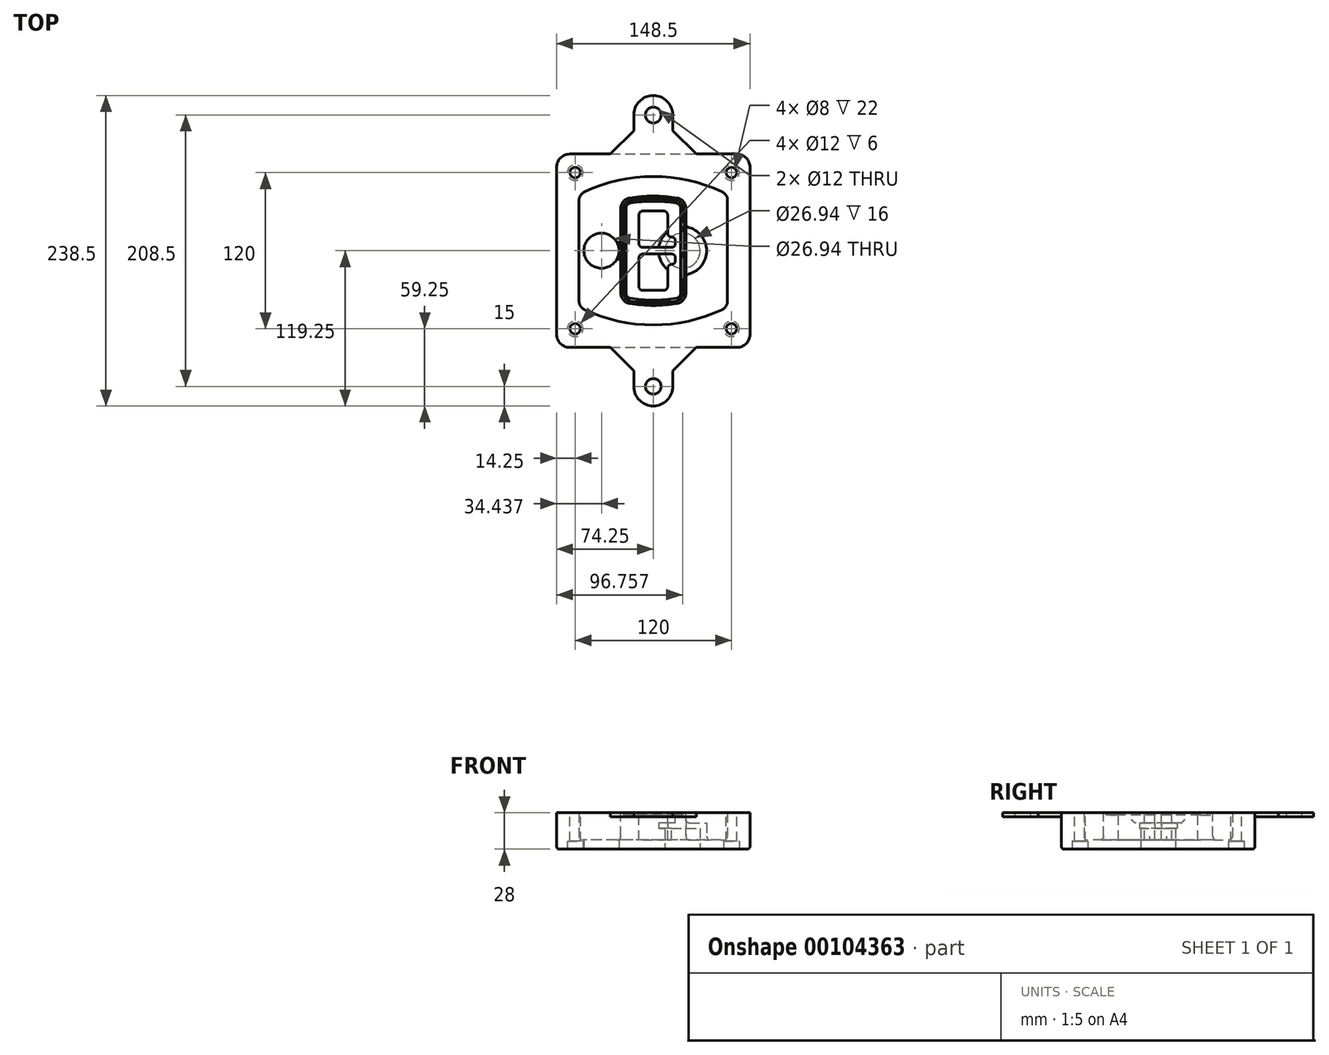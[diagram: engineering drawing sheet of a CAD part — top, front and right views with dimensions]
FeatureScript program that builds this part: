
annotation { "Feature Type Name" : "Feature", "Feature Type Description" : "" }
export const myFeature = defineFeature(function(context is Context, id is Id, definition is map)
    precondition{}
    {
        {
            var Q0;
            Q0=qCreatedBy(makeId("Top.planeOp"),FACE);
            var sketch = newSketch(context, id + "F0", { "sketchPlane" : qUnion([Q0])});
            skPoint(sketch, "E0.rect.middle", {"position": v(0, 0) * mm});
            skLineSegment(sketch, "E1.bottom", {"start": v(-64.25, -74.25) * mm, "end": v(64.25, -74.25) * mm});
            skLineSegment(sketch, "E1.top", {"start": v(-64.25, 74.25) * mm, "end": v(64.25, 74.25) * mm});
            skLineSegment(sketch, "E1.left", {"start": v(-74.25, -64.25) * mm, "end": v(-74.25, 64.25) * mm});
            skLineSegment(sketch, "E1.right", {"start": v(74.25, -64.25) * mm, "end": v(74.25, 64.25) * mm});
            skLineSegment(sketch, "E2", {"start": v(-74.25, 74.25) * mm, "end": v(74.25, -74.25) * mm, "construction": true});
            skLineSegment(sketch, "E3", {"start": v(74.25, 74.25) * mm, "end": v(-74.25, -74.25) * mm, "construction": true});
            skCircle(sketch, "E4", {"center": v(-60, 60) * mm, "radius": 4 * mm});
            skCircle(sketch, "E5", {"center": v(60, 60) * mm, "radius": 4 * mm});
            skCircle(sketch, "E6", {"center": v(60, -60) * mm, "radius": 4 * mm});
            skCircle(sketch, "E7", {"center": v(-60, -60) * mm, "radius": 4 * mm});
            skLineSegment(sketch, "E8", {"start": v(-60, 60) * mm, "end": v(60, 60) * mm, "construction": true});
            skLineSegment(sketch, "E9", {"start": v(60, 60) * mm, "end": v(60, -60) * mm, "construction": true});
            skLineSegment(sketch, "E10", {"start": v(60, -60) * mm, "end": v(-60, -60) * mm, "construction": true});
            skLineSegment(sketch, "E11", {"start": v(-60, -60) * mm, "end": v(-60, 60) * mm, "construction": true});
            skLineSegment(sketch, "E12", {"start": v(-60, 38.83) * mm, "end": v(-60, -38.83) * mm});
            skLineSegment(sketch, "E13", {"start": v(60, 38.83) * mm, "end": v(60, -38.83) * mm});
            skArc(sketch, "E14", {"start": v(54.26, 47.88) * mm, "mid": v(0, 60) * mm, "end": v(-54.26, 47.88) * mm});
            skArc(sketch, "E15", {"start": v(-54.26, -47.88) * mm, "mid": v(0, -60) * mm, "end": v(54.26, -47.88) * mm});
            skLineSegment(sketch, "E16", {"start": v(-60, 0) * mm, "end": v(60, 0) * mm, "construction": true});
            skPoint(sketch, "E17.visualSharp", {"position": v(-60, -45) * mm});
            skArc(sketch, "E17.filletArc", {"start": v(-60, -38.83) * mm, "mid": v(-58.44, -44.2) * mm, "end": v(-54.26, -47.88) * mm});
            skPoint(sketch, "E18.visualSharp", {"position": v(-60, 45) * mm});
            skArc(sketch, "E18.filletArc", {"start": v(-54.26, 47.88) * mm, "mid": v(-58.44, 44.2) * mm, "end": v(-60, 38.83) * mm});
            skPoint(sketch, "E19.visualSharp", {"position": v(60, 45) * mm});
            skArc(sketch, "E19.filletArc", {"start": v(60, 38.83) * mm, "mid": v(58.44, 44.2) * mm, "end": v(54.26, 47.88) * mm});
            skPoint(sketch, "E20.visualSharp", {"position": v(60, -45) * mm});
            skArc(sketch, "E20.filletArc", {"start": v(54.26, -47.88) * mm, "mid": v(58.44, -44.2) * mm, "end": v(60, -38.83) * mm});
            skPoint(sketch, "E21.visualSharp", {"position": v(-74.25, 74.25) * mm});
            skArc(sketch, "E21.filletArc", {"start": v(-64.25, 74.25) * mm, "mid": v(-71.32, 71.32) * mm, "end": v(-74.25, 64.25) * mm});
            skPoint(sketch, "E22.visualSharp", {"position": v(74.25, 74.25) * mm});
            skArc(sketch, "E22.filletArc", {"start": v(74.25, 64.25) * mm, "mid": v(71.32, 71.32) * mm, "end": v(64.25, 74.25) * mm});
            skPoint(sketch, "E23.visualSharp", {"position": v(74.25, -74.25) * mm});
            skArc(sketch, "E23.filletArc", {"start": v(64.25, -74.25) * mm, "mid": v(71.32, -71.32) * mm, "end": v(74.25, -64.25) * mm});
            skPoint(sketch, "E24.visualSharp", {"position": v(-74.25, -74.25) * mm});
            skArc(sketch, "E24.filletArc", {"start": v(-74.25, -64.25) * mm, "mid": v(-71.32, -71.32) * mm, "end": v(-64.25, -74.25) * mm});
            skArc(sketch, "E25.0", {"start": v(57, 38.83) * mm, "mid": v(55.9, 42.58) * mm, "end": v(52.98, 45.17) * mm});
            skLineSegment(sketch, "E25.1", {"start": v(57, 38.83) * mm, "end": v(57, -38.83) * mm});
            skArc(sketch, "E25.2", {"start": v(52.98, -45.17) * mm, "mid": v(55.9, -42.58) * mm, "end": v(57, -38.83) * mm});
            skArc(sketch, "E25.3", {"start": v(-52.98, -45.17) * mm, "mid": v(0, -57) * mm, "end": v(52.98, -45.17) * mm});
            skArc(sketch, "E25.4", {"start": v(-57, -38.83) * mm, "mid": v(-55.9, -42.58) * mm, "end": v(-52.98, -45.17) * mm});
            skArc(sketch, "E25.5", {"start": v(52.98, 45.17) * mm, "mid": v(0, 57) * mm, "end": v(-52.98, 45.17) * mm});
            skLineSegment(sketch, "E25.6", {"start": v(-57, 38.83) * mm, "end": v(-57, -38.83) * mm});
            skArc(sketch, "E25.7", {"start": v(-52.98, 45.17) * mm, "mid": v(-55.9, 42.58) * mm, "end": v(-57, 38.83) * mm});
            skArc(sketch, "E26.0", {"start": v(-55.96, 51.5) * mm, "mid": v(-61.82, 46.33) * mm, "end": v(-64, 38.83) * mm});
            skArc(sketch, "E26.1", {"start": v(55.96, 51.5) * mm, "mid": v(0, 64) * mm, "end": v(-55.96, 51.5) * mm});
            skArc(sketch, "E26.2", {"start": v(64, 38.83) * mm, "mid": v(61.82, 46.33) * mm, "end": v(55.96, 51.5) * mm});
            skLineSegment(sketch, "E26.3", {"start": v(64, 38.83) * mm, "end": v(64, -38.83) * mm});
            skArc(sketch, "E26.4", {"start": v(55.96, -51.5) * mm, "mid": v(61.82, -46.33) * mm, "end": v(64, -38.83) * mm});
            skLineSegment(sketch, "E26.5", {"start": v(-64, 38.83) * mm, "end": v(-64, -38.83) * mm});
            skArc(sketch, "E26.6", {"start": v(-55.96, -51.5) * mm, "mid": v(0, -64) * mm, "end": v(55.96, -51.5) * mm});
            skArc(sketch, "E26.7", {"start": v(-64, -38.83) * mm, "mid": v(-61.82, -46.33) * mm, "end": v(-55.96, -51.5) * mm});
            skSolve(sketch);
        }
        {
            var Q0;
            Q0=makeQuery(id+"F0.imprint","IMPRINT",FACE,{"disambiguationData":[TD([[makeQuery(id+"F0.imprint","IMPRINT",EDGE,{"derivedFrom":sQuery(id+"F0.wireOp",EDGE,"E1.bottom")}),1.0]])]});
            var Q1;
            Q1=makeQuery(id+"F0.imprint","IMPRINT",FACE,{"disambiguationData":[TD([[makeQuery(id+"F0.imprint","IMPRINT",EDGE,{"derivedFrom":sQuery(id+"F0.wireOp",EDGE,"E12")}),1.0]])]});
            var Q2;
            Q2=makeQuery(id+"F0.imprint","IMPRINT",FACE,{"disambiguationData":[TD([[makeQuery(id+"F0.imprint","IMPRINT",EDGE,{"derivedFrom":sQuery(id+"F0.wireOp",EDGE,"E25.0")}),1.0]])]});
            var Q3;
            Q3=makeQuery(id+"F0.imprint","IMPRINT",FACE,{"disambiguationData":[TD([[makeQuery(id+"F0.imprint","IMPRINT",EDGE,{"derivedFrom":sQuery(id+"F0.wireOp",EDGE,"E12")}),-1.0]])]});
            extrude(context, id + "F1", {"entities" : qUnion([Q0, Q1, Q2, Q3]), "oppositeDirection" : true, "depth" : 25 * mm});
        }
        {
            var Q0;
            Q0=makeQuery(id+"F0.imprint","IMPRINT",FACE,{"disambiguationData":[TD([[makeQuery(id+"F0.imprint","IMPRINT",EDGE,{"derivedFrom":sQuery(id+"F0.wireOp",EDGE,"E12")}),1.0]])]});
            extrude(context, id + "F2", {"entities" : qUnion([Q0]), "operationType" : NewBodyOperationType.ADD, "depth" : 3 * mm});
        }
        {
            var Q0;
            Q0=makeQuery(id+"F0.imprint","IMPRINT",FACE,{"disambiguationData":[TD([[makeQuery(id+"F0.imprint","IMPRINT",EDGE,{"derivedFrom":sQuery(id+"F0.wireOp",EDGE,"E25.0")}),1.0]])]});
            extrude(context, id + "F3", {"entities" : qUnion([Q0]), "operationType" : NewBodyOperationType.REMOVE, "oppositeDirection" : true, "depth" : 18 * mm});
        }
        {
            var Q0;
            Q0=makeQuery(id+"F2.opExtrude","CAP_FACE",FACE,{"disambiguationData":[OSD([sQuery(id+"F0.wireOp",EDGE,"E12"),sQuery(id+"F0.wireOp",EDGE,"E13"),sQuery(id+"F0.wireOp",EDGE,"E14"),sQuery(id+"F0.wireOp",EDGE,"E15"),sQuery(id+"F0.wireOp",EDGE,"E17.filletArc"),sQuery(id+"F0.wireOp",EDGE,"E18.filletArc"),sQuery(id+"F0.wireOp",EDGE,"E19.filletArc"),sQuery(id+"F0.wireOp",EDGE,"E20.filletArc"),sQuery(id+"F0.wireOp",EDGE,"E25.0"),sQuery(id+"F0.wireOp",EDGE,"E25.1"),sQuery(id+"F0.wireOp",EDGE,"E25.2"),sQuery(id+"F0.wireOp",EDGE,"E25.3"),sQuery(id+"F0.wireOp",EDGE,"E25.4"),sQuery(id+"F0.wireOp",EDGE,"E25.5"),sQuery(id+"F0.wireOp",EDGE,"E25.6"),sQuery(id+"F0.wireOp",EDGE,"E25.7")])],"isStart":false});
            var sketch = newSketch(context, id + "F4", { "sketchPlane" : qUnion([Q0])});
            skArc(sketch, "E27.0", {"start": v(-18.34, -40.45) * mm, "mid": v(0, -42) * mm, "end": v(18.34, -40.45) * mm});
            skArc(sketch, "E28.0", {"start": v(18.34, 40.45) * mm, "mid": v(0, 42) * mm, "end": v(-18.34, 40.45) * mm});
            skLineSegment(sketch, "E29", {"start": v(-25, 32.57) * mm, "end": v(-25, -32.57) * mm});
            skLineSegment(sketch, "E30", {"start": v(25, 32.57) * mm, "end": v(25, -32.57) * mm});
            skLineSegment(sketch, "E31", {"start": v(-25, 39.1) * mm, "end": v(25, 39.1) * mm, "construction": true});
            skLineSegment(sketch, "E32", {"start": v(-25, -39.1) * mm, "end": v(25, -39.1) * mm, "construction": true});
            skPoint(sketch, "E33.visualSharp", {"position": v(-25, 39.1) * mm});
            skArc(sketch, "E33.filletArc", {"start": v(-18.34, 40.45) * mm, "mid": v(-23.11, 37.73) * mm, "end": v(-25, 32.57) * mm});
            skPoint(sketch, "E34.visualSharp", {"position": v(25, 39.1) * mm});
            skArc(sketch, "E34.filletArc", {"start": v(25, 32.57) * mm, "mid": v(23.11, 37.73) * mm, "end": v(18.34, 40.45) * mm});
            skPoint(sketch, "E35.visualSharp", {"position": v(25, -39.1) * mm});
            skArc(sketch, "E35.filletArc", {"start": v(18.34, -40.45) * mm, "mid": v(23.11, -37.73) * mm, "end": v(25, -32.57) * mm});
            skPoint(sketch, "E36.visualSharp", {"position": v(-25, -39.1) * mm});
            skArc(sketch, "E36.filletArc", {"start": v(-25, -32.57) * mm, "mid": v(-23.11, -37.73) * mm, "end": v(-18.34, -40.45) * mm});
            skArc(sketch, "E37.0", {"start": v(52.98, 45.17) * mm, "mid": v(0, 57) * mm, "end": v(-52.98, 45.17) * mm});
            skArc(sketch, "E37.1", {"start": v(-52.98, 45.17) * mm, "mid": v(-55.9, 42.58) * mm, "end": v(-57, 38.83) * mm});
            skLineSegment(sketch, "E37.2", {"start": v(-57, 38.83) * mm, "end": v(-57, -38.83) * mm});
            skArc(sketch, "E37.3", {"start": v(-57, -38.83) * mm, "mid": v(-55.9, -42.58) * mm, "end": v(-52.98, -45.17) * mm});
            skArc(sketch, "E37.4", {"start": v(-52.98, -45.17) * mm, "mid": v(0, -57) * mm, "end": v(52.98, -45.17) * mm});
            skArc(sketch, "E37.5", {"start": v(52.98, -45.17) * mm, "mid": v(55.9, -42.58) * mm, "end": v(57, -38.83) * mm});
            skLineSegment(sketch, "E37.6", {"start": v(57, 38.83) * mm, "end": v(57, -38.83) * mm});
            skArc(sketch, "E37.7", {"start": v(57, 38.83) * mm, "mid": v(55.9, 42.58) * mm, "end": v(52.98, 45.17) * mm});
            skLineSegment(sketch, "E38.0", {"start": v(23, 32.57) * mm, "end": v(23, -32.57) * mm});
            skArc(sketch, "E38.1", {"start": v(18, -38.48) * mm, "mid": v(21.58, -36.44) * mm, "end": v(23, -32.57) * mm});
            skArc(sketch, "E38.2", {"start": v(-18, -38.48) * mm, "mid": v(0, -40) * mm, "end": v(18, -38.48) * mm});
            skArc(sketch, "E38.3", {"start": v(-23, -32.57) * mm, "mid": v(-21.58, -36.44) * mm, "end": v(-18, -38.48) * mm});
            skLineSegment(sketch, "E38.4", {"start": v(-23, 32.57) * mm, "end": v(-23, -32.57) * mm});
            skArc(sketch, "E38.5", {"start": v(23, 32.57) * mm, "mid": v(21.58, 36.44) * mm, "end": v(18, 38.48) * mm});
            skArc(sketch, "E38.6", {"start": v(-18, 38.48) * mm, "mid": v(-21.58, 36.44) * mm, "end": v(-23, 32.57) * mm});
            skArc(sketch, "E38.7", {"start": v(18, 38.48) * mm, "mid": v(0, 40) * mm, "end": v(-18, 38.48) * mm});
            skArc(sketch, "E39.0", {"start": v(21, 32.57) * mm, "mid": v(20.06, 35.15) * mm, "end": v(17.67, 36.5) * mm});
            skLineSegment(sketch, "E39.1", {"start": v(21, 32.57) * mm, "end": v(21, -32.57) * mm});
            skArc(sketch, "E39.2", {"start": v(17.67, -36.5) * mm, "mid": v(20.06, -35.15) * mm, "end": v(21, -32.57) * mm});
            skArc(sketch, "E39.3", {"start": v(-17.67, -36.5) * mm, "mid": v(0, -38) * mm, "end": v(17.67, -36.5) * mm});
            skArc(sketch, "E39.4", {"start": v(-21, -32.57) * mm, "mid": v(-20.06, -35.15) * mm, "end": v(-17.67, -36.5) * mm});
            skArc(sketch, "E39.5", {"start": v(17.67, 36.5) * mm, "mid": v(0, 38) * mm, "end": v(-17.67, 36.5) * mm});
            skLineSegment(sketch, "E39.6", {"start": v(-21, 32.57) * mm, "end": v(-21, -32.57) * mm});
            skArc(sketch, "E39.7", {"start": v(-17.67, 36.5) * mm, "mid": v(-20.06, 35.15) * mm, "end": v(-21, 32.57) * mm});
            skLineSegment(sketch, "E40", {"start": v(-25, 0) * mm, "end": v(25, 0) * mm, "construction": true});
            skLineSegment(sketch, "E41", {"start": v(-11, 5.5) * mm, "end": v(-11, 27.5) * mm});
            skLineSegment(sketch, "E42", {"start": v(-8, 30.5) * mm, "end": v(8, 30.5) * mm});
            skLineSegment(sketch, "E43", {"start": v(11, 27.5) * mm, "end": v(11, 13.5) * mm});
            skLineSegment(sketch, "E44", {"start": v(14, 10.5) * mm, "end": v(14, 10.5) * mm});
            skLineSegment(sketch, "E45", {"start": v(17, 7.5) * mm, "end": v(17, 5.5) * mm});
            skLineSegment(sketch, "E46", {"start": v(14, 2.5) * mm, "end": v(-8, 2.5) * mm});
            skPoint(sketch, "E47.visualSharp", {"position": v(-11, 30.5) * mm});
            skArc(sketch, "E47.filletArc", {"start": v(-8, 30.5) * mm, "mid": v(-10.12, 29.62) * mm, "end": v(-11, 27.5) * mm});
            skPoint(sketch, "E48.visualSharp", {"position": v(11, 30.5) * mm});
            skArc(sketch, "E48.filletArc", {"start": v(11, 27.5) * mm, "mid": v(10.12, 29.62) * mm, "end": v(8, 30.5) * mm});
            skPoint(sketch, "E49.visualSharp", {"position": v(11, 10.5) * mm});
            skArc(sketch, "E49.filletArc", {"start": v(11, 13.5) * mm, "mid": v(11.88, 11.38) * mm, "end": v(14, 10.5) * mm});
            skPoint(sketch, "E50.visualSharp", {"position": v(17, 10.5) * mm});
            skArc(sketch, "E50.filletArc", {"start": v(17, 7.5) * mm, "mid": v(16.12, 9.62) * mm, "end": v(14, 10.5) * mm});
            skPoint(sketch, "E51.visualSharp", {"position": v(17, 2.5) * mm});
            skArc(sketch, "E51.filletArc", {"start": v(14, 2.5) * mm, "mid": v(16.12, 3.38) * mm, "end": v(17, 5.5) * mm});
            skPoint(sketch, "E52.visualSharp", {"position": v(-11, 2.5) * mm});
            skArc(sketch, "E52.filletArc", {"start": v(-11, 5.5) * mm, "mid": v(-10.12, 3.38) * mm, "end": v(-8, 2.5) * mm});
            skLineSegment(sketch, "E53.0.MirrorCS", {"start": v(14, -2.5) * mm, "end": v(-8, -2.5) * mm});
            skArc(sketch, "E54.0.MirrorCS", {"start": v(-11, -5.5) * mm, "mid": v(-10.12, -3.38) * mm, "end": v(-8, -2.5) * mm});
            skLineSegment(sketch, "E55.0.MirrorCS", {"start": v(-11, -5.5) * mm, "end": v(-11, -27.5) * mm});
            skArc(sketch, "E56.0.MirrorCS", {"start": v(-8, -30.5) * mm, "mid": v(-10.12, -29.62) * mm, "end": v(-11, -27.5) * mm});
            skLineSegment(sketch, "E57.0.MirrorCS", {"start": v(-8, -30.5) * mm, "end": v(8, -30.5) * mm});
            skArc(sketch, "E58.0.MirrorCS", {"start": v(11, -27.5) * mm, "mid": v(10.12, -29.62) * mm, "end": v(8, -30.5) * mm});
            skLineSegment(sketch, "E59.0.MirrorCS", {"start": v(11, -27.5) * mm, "end": v(11, -13.5) * mm});
            skArc(sketch, "E60.0.MirrorCS", {"start": v(11, -13.5) * mm, "mid": v(11.88, -11.38) * mm, "end": v(14, -10.5) * mm});
            skArc(sketch, "E61.0.MirrorCS", {"start": v(17, -7.5) * mm, "mid": v(16.12, -9.62) * mm, "end": v(14, -10.5) * mm});
            skLineSegment(sketch, "E62.0.MirrorCS", {"start": v(17, -7.5) * mm, "end": v(17, -5.5) * mm});
            skArc(sketch, "E63.0.MirrorCS", {"start": v(14, -2.5) * mm, "mid": v(16.12, -3.38) * mm, "end": v(17, -5.5) * mm});
            skSolve(sketch);
        }
        {
            var Q0;
            Q0=makeQuery(id+"F4.imprint","IMPRINT",FACE,{"disambiguationData":[TD([[makeQuery(id+"F4.imprint","IMPRINT",EDGE,{"derivedFrom":sQuery(id+"F4.wireOp",EDGE,"E27.0")}),1.0]])]});
            var Q1;
            Q1=makeQuery(id+"F4.imprint","IMPRINT",FACE,{"disambiguationData":[TD([[makeQuery(id+"F4.imprint","IMPRINT",EDGE,{"derivedFrom":sQuery(id+"F4.wireOp",EDGE,"E38.0")}),-1.0]])]});
            var Q2;
            Q2=makeQuery(id+"F4.imprint","IMPRINT",FACE,{"disambiguationData":[TD([[makeQuery(id+"F4.imprint","IMPRINT",EDGE,{"derivedFrom":sQuery(id+"F4.wireOp",EDGE,"E39.0")}),1.0]])]});
            extrude(context, id + "F5", {"entities" : qUnion([Q0, Q1, Q2]), "operationType" : NewBodyOperationType.ADD, "endBound" : BoundingType.UP_TO_NEXT, "oppositeDirection" : true, "depth" : 25 * mm});
        }
        {
            var Q0;
            Q0=makeQuery(id+"F4.imprint","IMPRINT",FACE,{"disambiguationData":[TD([[makeQuery(id+"F4.imprint","IMPRINT",EDGE,{"derivedFrom":sQuery(id+"F4.wireOp",EDGE,"E38.0")}),-1.0]])]});
            extrude(context, id + "F6", {"entities" : qUnion([Q0]), "operationType" : NewBodyOperationType.REMOVE, "oppositeDirection" : true, "depth" : 2 * mm});
        }
        {
            var Q0;
            Q0=makeQuery(id+"F1.opExtrude","CAP_FACE",FACE,{"disambiguationData":[OSD([sQuery(id+"F0.wireOp",EDGE,"E1.bottom"),sQuery(id+"F0.wireOp",EDGE,"E1.top"),sQuery(id+"F0.wireOp",EDGE,"E1.left"),sQuery(id+"F0.wireOp",EDGE,"E1.right"),sQuery(id+"F0.wireOp",EDGE,"E4"),sQuery(id+"F0.wireOp",EDGE,"E5"),sQuery(id+"F0.wireOp",EDGE,"E6"),sQuery(id+"F0.wireOp",EDGE,"E7"),sQuery(id+"F0.wireOp",EDGE,"E21.filletArc"),sQuery(id+"F0.wireOp",EDGE,"E22.filletArc"),sQuery(id+"F0.wireOp",EDGE,"E23.filletArc"),sQuery(id+"F0.wireOp",EDGE,"E24.filletArc")])],"isStart":false});
            var sketch = newSketch(context, id + "F7", { "sketchPlane" : qUnion([Q0])});
            skCircle(sketch, "E64", {"center": v(22.5, 0) * mm, "radius": 13.47 * mm});
            skCircle(sketch, "E65", {"center": v(-39.81, 0) * mm, "radius": 13.47 * mm});
            skLineSegment(sketch, "E66", {"start": v(74.25, 0) * mm, "end": v(-74.25, 0) * mm});
            skCircle(sketch, "E67", {"center": v(22.5, 0) * mm, "radius": 18.47 * mm});
            skCircle(sketch, "E68", {"center": v(60, -60) * mm, "radius": 6 * mm});
            skCircle(sketch, "E69", {"center": v(-60, -60) * mm, "radius": 6 * mm});
            skCircle(sketch, "E70", {"center": v(-60, 60) * mm, "radius": 6 * mm});
            skCircle(sketch, "E71", {"center": v(60, 60) * mm, "radius": 6 * mm});
            skSolve(sketch);
        }
        {
            var Q0;
            {var subQ1=sQuery(id+"F7.wireOp",EDGE,"E66");var subQ4=sQuery(id+"F7.wireOp",EDGE,"E64");var subQ6=makeQuery(id+"F7.imprint","INTERSECT",VERTEX,{"disambiguationData":[OD(0.0)],"derivedFrom":[subQ4,subQ1]});Q0=makeQuery(id+"F7.imprint","IMPRINT",FACE,{"disambiguationData":[TD([[makeQuery(id+"F7.imprint","IMPRINT",EDGE,{"disambiguationData":[TD([[subQ6,-1.0]])],"derivedFrom":subQ4}),-1.0]])]});}
            var Q1;
            {var subQ0=sQuery(id+"F7.wireOp",EDGE,"E66");var subQ1=sQuery(id+"F7.wireOp",EDGE,"E64");var subQ3=makeQuery(id+"F7.imprint","INTERSECT",VERTEX,{"disambiguationData":[OD(0.0)],"derivedFrom":[subQ1,subQ0]});Q1=makeQuery(id+"F7.imprint","IMPRINT",FACE,{"disambiguationData":[TD([[makeQuery(id+"F7.imprint","IMPRINT",EDGE,{"disambiguationData":[TD([[subQ3,-1.0]])],"derivedFrom":subQ1}),1.0]])]});}
            var Q2;
            {var subQ0=sQuery(id+"F7.wireOp",EDGE,"E66");var subQ1=sQuery(id+"F7.wireOp",EDGE,"E64");var subQ3=makeQuery(id+"F7.imprint","INTERSECT",VERTEX,{"disambiguationData":[OD(0.0)],"derivedFrom":[subQ1,subQ0]});Q2=makeQuery(id+"F7.imprint","IMPRINT",FACE,{"disambiguationData":[TD([[makeQuery(id+"F7.imprint","IMPRINT",EDGE,{"disambiguationData":[TD([[subQ3,1.0]])],"derivedFrom":subQ1}),1.0]])]});}
            var Q3;
            {var subQ1=sQuery(id+"F7.wireOp",EDGE,"E66");var subQ4=sQuery(id+"F7.wireOp",EDGE,"E64");var subQ6=makeQuery(id+"F7.imprint","INTERSECT",VERTEX,{"disambiguationData":[OD(0.0)],"derivedFrom":[subQ4,subQ1]});Q3=makeQuery(id+"F7.imprint","IMPRINT",FACE,{"disambiguationData":[TD([[makeQuery(id+"F7.imprint","IMPRINT",EDGE,{"disambiguationData":[TD([[subQ6,1.0]])],"derivedFrom":subQ4}),-1.0]])]});}
            extrude(context, id + "F8", {"entities" : qUnion([Q0, Q1, Q2, Q3]), "operationType" : NewBodyOperationType.ADD, "oppositeDirection" : true, "depth" : 20 * mm});
        }
        {
            var Q0;
            {var subQ0=sQuery(id+"F7.wireOp",EDGE,"E66");var subQ1=sQuery(id+"F7.wireOp",EDGE,"E64");var subQ3=makeQuery(id+"F7.imprint","INTERSECT",VERTEX,{"disambiguationData":[OD(0.0)],"derivedFrom":[subQ1,subQ0]});Q0=makeQuery(id+"F7.imprint","IMPRINT",FACE,{"disambiguationData":[TD([[makeQuery(id+"F7.imprint","IMPRINT",EDGE,{"disambiguationData":[TD([[subQ3,-1.0]])],"derivedFrom":subQ1}),1.0]])]});}
            var Q1;
            {var subQ0=sQuery(id+"F7.wireOp",EDGE,"E66");var subQ1=sQuery(id+"F7.wireOp",EDGE,"E64");var subQ3=makeQuery(id+"F7.imprint","INTERSECT",VERTEX,{"disambiguationData":[OD(0.0)],"derivedFrom":[subQ1,subQ0]});Q1=makeQuery(id+"F7.imprint","IMPRINT",FACE,{"disambiguationData":[TD([[makeQuery(id+"F7.imprint","IMPRINT",EDGE,{"disambiguationData":[TD([[subQ3,1.0]])],"derivedFrom":subQ1}),1.0]])]});}
            extrude(context, id + "F9", {"entities" : qUnion([Q0, Q1]), "operationType" : NewBodyOperationType.REMOVE, "oppositeDirection" : true, "depth" : 16 * mm});
        }
        {
            var Q0;
            {var subQ0=sQuery(id+"F7.wireOp",EDGE,"E66");var subQ1=sQuery(id+"F7.wireOp",EDGE,"E65");var subQ3=makeQuery(id+"F7.imprint","INTERSECT",VERTEX,{"disambiguationData":[OD(0.0)],"derivedFrom":[subQ1,subQ0]});Q0=makeQuery(id+"F7.imprint","IMPRINT",FACE,{"disambiguationData":[TD([[makeQuery(id+"F7.imprint","IMPRINT",EDGE,{"disambiguationData":[TD([[subQ3,-1.0]])],"derivedFrom":subQ1}),1.0]])]});}
            var Q1;
            {var subQ0=sQuery(id+"F7.wireOp",EDGE,"E66");var subQ1=sQuery(id+"F7.wireOp",EDGE,"E65");var subQ3=makeQuery(id+"F7.imprint","INTERSECT",VERTEX,{"disambiguationData":[OD(0.0)],"derivedFrom":[subQ1,subQ0]});Q1=makeQuery(id+"F7.imprint","IMPRINT",FACE,{"disambiguationData":[TD([[makeQuery(id+"F7.imprint","IMPRINT",EDGE,{"disambiguationData":[TD([[subQ3,1.0]])],"derivedFrom":subQ1}),1.0]])]});}
            extrude(context, id + "F10", {"entities" : qUnion([Q0, Q1]), "operationType" : NewBodyOperationType.REMOVE, "oppositeDirection" : true, "depth" : 25 * mm});
        }
        {
            var Q0;
            Q0=makeQuery(id+"F7.imprint","IMPRINT",FACE,{"disambiguationData":[TD([[makeQuery(id+"F7.imprint","IMPRINT",EDGE,{"derivedFrom":sQuery(id+"F7.wireOp",EDGE,"E68")}),1.0]])]});
            var Q1;
            Q1=makeQuery(id+"F7.imprint","IMPRINT",FACE,{"disambiguationData":[TD([[makeQuery(id+"F7.imprint","IMPRINT",EDGE,{"derivedFrom":makeQuery(id+"F1.opExtrude","CAP_EDGE",EDGE,{"disambiguationData":[OSD([sQuery(id+"F0.wireOp",EDGE,"E5")])],"isStart":false})}),-1.0]])]});
            var Q2;
            Q2=makeQuery(id+"F7.imprint","IMPRINT",FACE,{"disambiguationData":[TD([[makeQuery(id+"F7.imprint","IMPRINT",EDGE,{"derivedFrom":sQuery(id+"F7.wireOp",EDGE,"E69")}),1.0]])]});
            var Q3;
            Q3=makeQuery(id+"F7.imprint","IMPRINT",FACE,{"disambiguationData":[TD([[makeQuery(id+"F7.imprint","IMPRINT",EDGE,{"derivedFrom":makeQuery(id+"F1.opExtrude","CAP_EDGE",EDGE,{"disambiguationData":[OSD([sQuery(id+"F0.wireOp",EDGE,"E4")])],"isStart":false})}),-1.0]])]});
            var Q4;
            Q4=makeQuery(id+"F7.imprint","IMPRINT",FACE,{"disambiguationData":[TD([[makeQuery(id+"F7.imprint","IMPRINT",EDGE,{"derivedFrom":sQuery(id+"F7.wireOp",EDGE,"E70")}),1.0]])]});
            var Q5;
            Q5=makeQuery(id+"F7.imprint","IMPRINT",FACE,{"disambiguationData":[TD([[makeQuery(id+"F7.imprint","IMPRINT",EDGE,{"derivedFrom":makeQuery(id+"F1.opExtrude","CAP_EDGE",EDGE,{"disambiguationData":[OSD([sQuery(id+"F0.wireOp",EDGE,"E7")])],"isStart":false})}),-1.0]])]});
            var Q6;
            Q6=makeQuery(id+"F7.imprint","IMPRINT",FACE,{"disambiguationData":[TD([[makeQuery(id+"F7.imprint","IMPRINT",EDGE,{"derivedFrom":sQuery(id+"F7.wireOp",EDGE,"E71")}),1.0]])]});
            var Q7;
            Q7=makeQuery(id+"F7.imprint","IMPRINT",FACE,{"disambiguationData":[TD([[makeQuery(id+"F7.imprint","IMPRINT",EDGE,{"derivedFrom":makeQuery(id+"F1.opExtrude","CAP_EDGE",EDGE,{"disambiguationData":[OSD([sQuery(id+"F0.wireOp",EDGE,"E6")])],"isStart":false})}),-1.0]])]});
            extrude(context, id + "F11", {"entities" : qUnion([Q0, Q1, Q2, Q3, Q4, Q5, Q6, Q7]), "operationType" : NewBodyOperationType.REMOVE, "oppositeDirection" : true, "depth" : 6 * mm});
        }
        {
            var Q0;
            Q0=makeQuery(id+"F9.boolean.opBoolean","COPY",FACE,{"derivedFrom":makeQuery(id+"F9.opExtrude","CAP_FACE",FACE,{"disambiguationData":[OSD([sQuery(id+"F7.wireOp",EDGE,"E64")])],"isStart":false})});
            var sketch = newSketch(context, id + "F12", { "sketchPlane" : qUnion([Q0])});
            skArc(sketch, "E72.0", {"start": v(11, 14.45) * mm, "mid": v(6.45, 9.13) * mm, "end": v(4.2, 2.5) * mm});
            skArc(sketch, "E72.1", {"start": v(4.2, -2.5) * mm, "mid": v(6.45, -9.13) * mm, "end": v(11, -14.45) * mm});
            skLineSegment(sketch, "E73", {"start": v(4.2, -2.5) * mm, "end": v(14, -2.5) * mm});
            skLineSegment(sketch, "E74.0", {"start": v(14, 2.5) * mm, "end": v(4.2, 2.5) * mm});
            skArc(sketch, "E74.1", {"start": v(14, 2.5) * mm, "mid": v(16.12, 3.38) * mm, "end": v(17, 5.5) * mm});
            skLineSegment(sketch, "E74.2", {"start": v(17, 7.5) * mm, "end": v(17, 5.5) * mm});
            skArc(sketch, "E74.3", {"start": v(17, 7.5) * mm, "mid": v(16.12, 9.62) * mm, "end": v(14, 10.5) * mm});
            skArc(sketch, "E74.4", {"start": v(11, 13.5) * mm, "mid": v(11.88, 11.38) * mm, "end": v(14, 10.5) * mm});
            skLineSegment(sketch, "E74.5", {"start": v(11, 14.45) * mm, "end": v(11, 13.5) * mm});
            skLineSegment(sketch, "E74.7", {"start": v(14, -2.5) * mm, "end": v(4.2, -2.5) * mm});
            skArc(sketch, "E74.8", {"start": v(14, -2.5) * mm, "mid": v(16.12, -3.38) * mm, "end": v(17, -5.5) * mm});
            skLineSegment(sketch, "E74.9", {"start": v(17, -7.5) * mm, "end": v(17, -5.5) * mm});
            skArc(sketch, "E74.10", {"start": v(17, -7.5) * mm, "mid": v(16.12, -9.62) * mm, "end": v(14, -10.5) * mm});
            skArc(sketch, "E74.11", {"start": v(11, -13.5) * mm, "mid": v(11.88, -11.38) * mm, "end": v(14, -10.5) * mm});
            skLineSegment(sketch, "E74.12", {"start": v(11, -14.45) * mm, "end": v(11, -13.5) * mm});
            skPoint(sketch, "E75.orphan", {"position": v(11, -27.5) * mm});
            skPoint(sketch, "E76.orphan", {"position": v(-8, -2.5) * mm});
            skPoint(sketch, "E77.orphan", {"position": v(-8, 2.5) * mm});
            skPoint(sketch, "E78.orphan", {"position": v(11, 27.5) * mm});
            skSolve(sketch);
        }
        {
            var Q0;
            {var subQ7=sQuery(id+"F12.wireOp",EDGE,"E72.0");var subQ14=sQuery(id+"F12.wireOp",EDGE,"E72.1");var subQ16=sQuery(id+"F12.wireOp",EDGE,"E74.1");var subQ18=sQuery(id+"F12.wireOp",EDGE,"E74.8");Q0=qUnion([makeQuery(id+"F12.imprint","IMPRINT",FACE,{"disambiguationData":[TD([[makeQuery(id+"F12.imprint","IMPRINT",EDGE,{"derivedFrom":subQ7}),1.0]])]}),makeQuery(id+"F12.imprint","IMPRINT",FACE,{"disambiguationData":[TD([[makeQuery(id+"F12.imprint","IMPRINT",EDGE,{"derivedFrom":subQ14}),1.0]])]}),makeQuery(id+"F12.imprint","IMPRINT",FACE,{"disambiguationData":[TD([[makeQuery(id+"F12.imprint","IMPRINT",EDGE,{"derivedFrom":subQ16}),1.0]])]}),makeQuery(id+"F12.imprint","IMPRINT",FACE,{"disambiguationData":[TD([[makeQuery(id+"F12.imprint","IMPRINT",EDGE,{"derivedFrom":subQ18}),-1.0]])]})]);}
            var Q1;
            Q1=makeQuery(id+"F5.boolean.opBoolean","SPLIT",FACE,{"disambiguationData":[TD([makeQuery(id+"F5.opExtrude","SWEPT_FACE",FACE,{"disambiguationData":[OSD([sQuery(id+"F4.wireOp",EDGE,"E41")])]})])],"derivedFrom":makeQuery(id+"F3.boolean.opBoolean","COPY",FACE,{"derivedFrom":makeQuery(id+"F3.opExtrude","CAP_FACE",FACE,{"disambiguationData":[OSD([sQuery(id+"F0.wireOp",EDGE,"E25.0"),sQuery(id+"F0.wireOp",EDGE,"E25.1"),sQuery(id+"F0.wireOp",EDGE,"E25.2"),sQuery(id+"F0.wireOp",EDGE,"E25.3"),sQuery(id+"F0.wireOp",EDGE,"E25.4"),sQuery(id+"F0.wireOp",EDGE,"E25.5"),sQuery(id+"F0.wireOp",EDGE,"E25.6"),sQuery(id+"F0.wireOp",EDGE,"E25.7")])],"isStart":false})})});
            extrude(context, id + "F13", {"entities" : qUnion([Q0]), "operationType" : NewBodyOperationType.REMOVE, "endBound" : BoundingType.UP_TO_SURFACE, "endBoundEntityFace" : qUnion([Q1]), "depth" : 25 * mm});
        }
        {
            var Q0;
            Q0=makeQuery(id+"F3.boolean.opBoolean","COPY",EDGE,{"derivedFrom":makeQuery(id+"F3.opExtrude","CAP_EDGE",EDGE,{"disambiguationData":[OSD([sQuery(id+"F0.wireOp",EDGE,"E25.6")])],"isStart":false})});
            var Q1;
            Q1=makeQuery(id+"F8.boolean.opBoolean","INTERSECT",EDGE,{"derivedFrom":[makeQuery(id+"F5.opExtrude","SWEPT_FACE",FACE,{"disambiguationData":[OSD([sQuery(id+"F4.wireOp",EDGE,"E30")])]}),makeQuery(id+"F8.opExtrude","CAP_FACE",FACE,{"disambiguationData":[OSD([sQuery(id+"F7.wireOp",EDGE,"E67")])],"isStart":false})]});
            var Q2;
            Q2=makeQuery(id+"F8.boolean.opBoolean","INTERSECT",EDGE,{"disambiguationData":[OD(1.0)],"derivedFrom":[makeQuery(id+"F5.opExtrude","SWEPT_FACE",FACE,{"disambiguationData":[OSD([sQuery(id+"F4.wireOp",EDGE,"E30")])]}),makeQuery(id+"F8.opExtrude","SWEPT_FACE",FACE,{"disambiguationData":[OSD([sQuery(id+"F7.wireOp",EDGE,"E67")])]})]});
            var Q3;
            {var subQ0=sQuery(id+"F4.wireOp",EDGE,"E30");Q3=makeQuery(id+"F8.boolean.opBoolean","SPLIT",EDGE,{"disambiguationData":[TD([makeQuery(id+"F5.opExtrude","SWEPT_FACE",FACE,{"disambiguationData":[OSD([sQuery(id+"F4.wireOp",EDGE,"E35.filletArc")])]})])],"derivedFrom":makeQuery(id+"F5.opExtrude","CAP_EDGE",EDGE,{"disambiguationData":[OSD([subQ0])],"isStart":false})});}
            var Q4;
            {var subQ0=sQuery(id+"F0.wireOp",EDGE,"E25.7");var subQ1=sQuery(id+"F0.wireOp",EDGE,"E25.1");var subQ2=sQuery(id+"F0.wireOp",EDGE,"E25.6");var subQ3=sQuery(id+"F0.wireOp",EDGE,"E25.5");var subQ4=sQuery(id+"F0.wireOp",EDGE,"E25.4");var subQ5=sQuery(id+"F0.wireOp",EDGE,"E25.0");var subQ6=sQuery(id+"F0.wireOp",EDGE,"E25.2");var subQ7=sQuery(id+"F0.wireOp",EDGE,"E25.3");Q4=makeQuery(id+"F8.boolean.opBoolean","INTERSECT",EDGE,{"derivedFrom":[makeQuery(id+"F5.boolean.opBoolean","SPLIT",FACE,{"disambiguationData":[TD([makeQuery(id+"F2.opExtrude","SWEPT_FACE",FACE,{"disambiguationData":[OSD([subQ5])]})])],"derivedFrom":makeQuery(id+"F3.boolean.opBoolean","COPY",FACE,{"derivedFrom":makeQuery(id+"F3.opExtrude","CAP_FACE",FACE,{"disambiguationData":[OSD([subQ5,subQ1,subQ6,subQ7,subQ4,subQ3,subQ2,subQ0])],"isStart":false})})}),makeQuery(id+"F8.opExtrude","SWEPT_FACE",FACE,{"disambiguationData":[OSD([sQuery(id+"F7.wireOp",EDGE,"E67")])]})]});}
            var Q5;
            Q5=makeQuery(id+"F8.boolean.opBoolean","INTERSECT",EDGE,{"disambiguationData":[OD(0.0)],"derivedFrom":[makeQuery(id+"F5.opExtrude","SWEPT_FACE",FACE,{"disambiguationData":[OSD([sQuery(id+"F4.wireOp",EDGE,"E30")])]}),makeQuery(id+"F8.opExtrude","SWEPT_FACE",FACE,{"disambiguationData":[OSD([sQuery(id+"F7.wireOp",EDGE,"E67")])]})]});
            fillet(context, id + "F14", {"entities" : qUnion([Q0, Q1, Q2, Q3, Q4, Q5]), "radius" : 3 * mm, "tangentPropagation" : true, "allowEdgeOverflow" : false});
        }
        {
            var Q0;
            Q0=makeQuery(id+"F1.opExtrude","CAP_EDGE",EDGE,{"disambiguationData":[OSD([sQuery(id+"F0.wireOp",EDGE,"E1.bottom")])],"isStart":false});
            fillet(context, id + "F15", {"entities" : qUnion([Q0]), "radius" : 2 * mm, "tangentPropagation" : true, "allowEdgeOverflow" : false});
        }
        {
            var Q0;
            {var subQ0=sQuery(id+"F0.wireOp",EDGE,"E22.filletArc");var subQ1=sQuery(id+"F0.wireOp",EDGE,"E7");var subQ2=sQuery(id+"F0.wireOp",EDGE,"E6");var subQ3=sQuery(id+"F0.wireOp",EDGE,"E5");var subQ4=sQuery(id+"F0.wireOp",EDGE,"E4");var subQ5=sQuery(id+"F0.wireOp",EDGE,"E1.bottom");var subQ6=sQuery(id+"F0.wireOp",EDGE,"E21.filletArc");var subQ7=sQuery(id+"F0.wireOp",EDGE,"E1.top");var subQ8=sQuery(id+"F0.wireOp",EDGE,"E1.left");var subQ9=sQuery(id+"F0.wireOp",EDGE,"E1.right");var subQ10=sQuery(id+"F0.wireOp",EDGE,"E23.filletArc");var subQ11=sQuery(id+"F0.wireOp",EDGE,"E24.filletArc");Q0=makeQuery(id+"F2.boolean.opBoolean","SPLIT",FACE,{"disambiguationData":[TD([makeQuery(id+"F1.opExtrude","SWEPT_FACE",FACE,{"disambiguationData":[OSD([subQ5])]})])],"derivedFrom":makeQuery(id+"F1.opExtrude","CAP_FACE",FACE,{"disambiguationData":[OSD([subQ5,subQ7,subQ8,subQ9,subQ4,subQ3,subQ2,subQ1,subQ6,subQ0,subQ10,subQ11])],"isStart":true})});}
            var sketch = newSketch(context, id + "F16", { "sketchPlane" : qUnion([Q0])});
            skCircle(sketch, "E79", {"center": v(0, 104.25) * mm, "radius": 6 * mm});
            skLineSegment(sketch, "E80", {"start": v(-33, 74.25) * mm, "end": v(-15, 92.25) * mm});
            skLineSegment(sketch, "E81", {"start": v(-15, 104.25) * mm, "end": v(-15, 92.25) * mm});
            skArc(sketch, "E82", {"start": v(15, 104.25) * mm, "mid": v(0, 119.25) * mm, "end": v(-15, 104.25) * mm});
            skLineSegment(sketch, "E83", {"start": v(15, 104.25) * mm, "end": v(15, 92.25) * mm});
            skLineSegment(sketch, "E84", {"start": v(15, 92.25) * mm, "end": v(33, 74.25) * mm});
            skLineSegment(sketch, "E85.MirrorCS", {"start": v(-33, -74.25) * mm, "end": v(-15, -92.25) * mm});
            skLineSegment(sketch, "E86.MirrorCS", {"start": v(-15, -104.25) * mm, "end": v(-15, -92.25) * mm});
            skArc(sketch, "E87.MirrorCS", {"start": v(15, -104.25) * mm, "mid": v(0, -119.25) * mm, "end": v(-15, -104.25) * mm});
            skLineSegment(sketch, "E88.MirrorCS", {"start": v(15, -104.25) * mm, "end": v(15, -92.25) * mm});
            skLineSegment(sketch, "E89.MirrorCS", {"start": v(15, -92.25) * mm, "end": v(33, -74.25) * mm});
            skCircle(sketch, "E90.MirrorC", {"center": v(0, -104.25) * mm, "radius": 6 * mm});
            skSolve(sketch);
        }
        {
            var Q0;
            {var subQ0=sQuery(id+"F16.wireOp",EDGE,"E85.MirrorCS");Q0=makeQuery(id+"F16.imprint","IMPRINT",FACE,{"disambiguationData":[TD([[makeQuery(id+"F16.imprint","IMPRINT",EDGE,{"derivedFrom":subQ0}),1.0]])]});}
            var Q1;
            Q1=makeQuery(id+"F16.imprint","IMPRINT",FACE,{"disambiguationData":[TD([[makeQuery(id+"F16.imprint","IMPRINT",EDGE,{"derivedFrom":makeQuery(id+"F1.opExtrude","CAP_EDGE",EDGE,{"disambiguationData":[OSD([sQuery(id+"F0.wireOp",EDGE,"E1.left")])],"isStart":true})}),-1.0]])]});
            var Q2;
            Q2=makeQuery(id+"F16.imprint","IMPRINT",FACE,{"disambiguationData":[TD([[makeQuery(id+"F16.imprint","IMPRINT",EDGE,{"derivedFrom":sQuery(id+"F16.wireOp",EDGE,"E79")}),-1.0]])]});
            var Q3;
            Q3=makeQuery(id+"F2.opExtrude","CAP_FACE",FACE,{"disambiguationData":[OSD([sQuery(id+"F0.wireOp",EDGE,"E12"),sQuery(id+"F0.wireOp",EDGE,"E13"),sQuery(id+"F0.wireOp",EDGE,"E14"),sQuery(id+"F0.wireOp",EDGE,"E15"),sQuery(id+"F0.wireOp",EDGE,"E17.filletArc"),sQuery(id+"F0.wireOp",EDGE,"E18.filletArc"),sQuery(id+"F0.wireOp",EDGE,"E19.filletArc"),sQuery(id+"F0.wireOp",EDGE,"E20.filletArc"),sQuery(id+"F0.wireOp",EDGE,"E25.0"),sQuery(id+"F0.wireOp",EDGE,"E25.1"),sQuery(id+"F0.wireOp",EDGE,"E25.2"),sQuery(id+"F0.wireOp",EDGE,"E25.3"),sQuery(id+"F0.wireOp",EDGE,"E25.4"),sQuery(id+"F0.wireOp",EDGE,"E25.5"),sQuery(id+"F0.wireOp",EDGE,"E25.6"),sQuery(id+"F0.wireOp",EDGE,"E25.7")])],"isStart":false});
            extrude(context, id + "F17", {"entities" : qUnion([Q0, Q1, Q2]), "operationType" : NewBodyOperationType.ADD, "endBound" : BoundingType.UP_TO_SURFACE, "endBoundEntityFace" : qUnion([Q3]), "depth" : 25 * mm});
        }
    });
